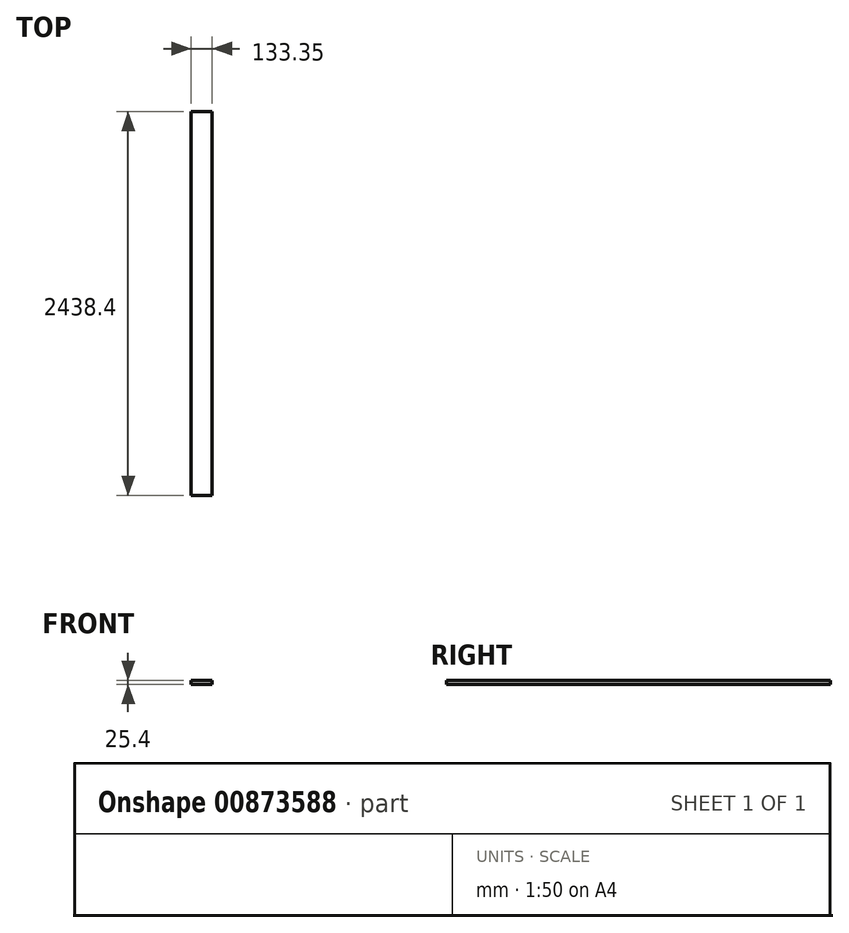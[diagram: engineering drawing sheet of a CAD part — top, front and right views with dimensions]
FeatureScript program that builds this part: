
annotation { "Feature Type Name" : "Feature", "Feature Type Description" : "" }
export const myFeature = defineFeature(function(context is Context, id is Id, definition is map)
    precondition{}
    {
        {
            var Q0;
            Q0=qCreatedBy(makeId("Top.planeOp"),FACE);
            var sketch = newSketch(context, id + "F0", { "sketchPlane" : qUnion([Q0])});
            skLineSegment(sketch, "E0.bottom", {"start": v(0, 0) * mm, "end": v(133.35, 0) * mm});
            skLineSegment(sketch, "E0.top", {"start": v(0, 2438.4) * mm, "end": v(133.35, 2438.4) * mm});
            skLineSegment(sketch, "E0.left", {"start": v(0, 0) * mm, "end": v(0, 2438.4) * mm});
            skLineSegment(sketch, "E0.right", {"start": v(133.35, 0) * mm, "end": v(133.35, 2438.4) * mm});
            skSolve(sketch);
        }
        {
            var Q0;
            Q0=qSketchRegion(id+"F0",true);
            extrude(context, id + "F1", {"entities" : qUnion([Q0]), "depth" : 25.4 * mm, "offsetDistance" : 25.4 * mm});
        }
    });
